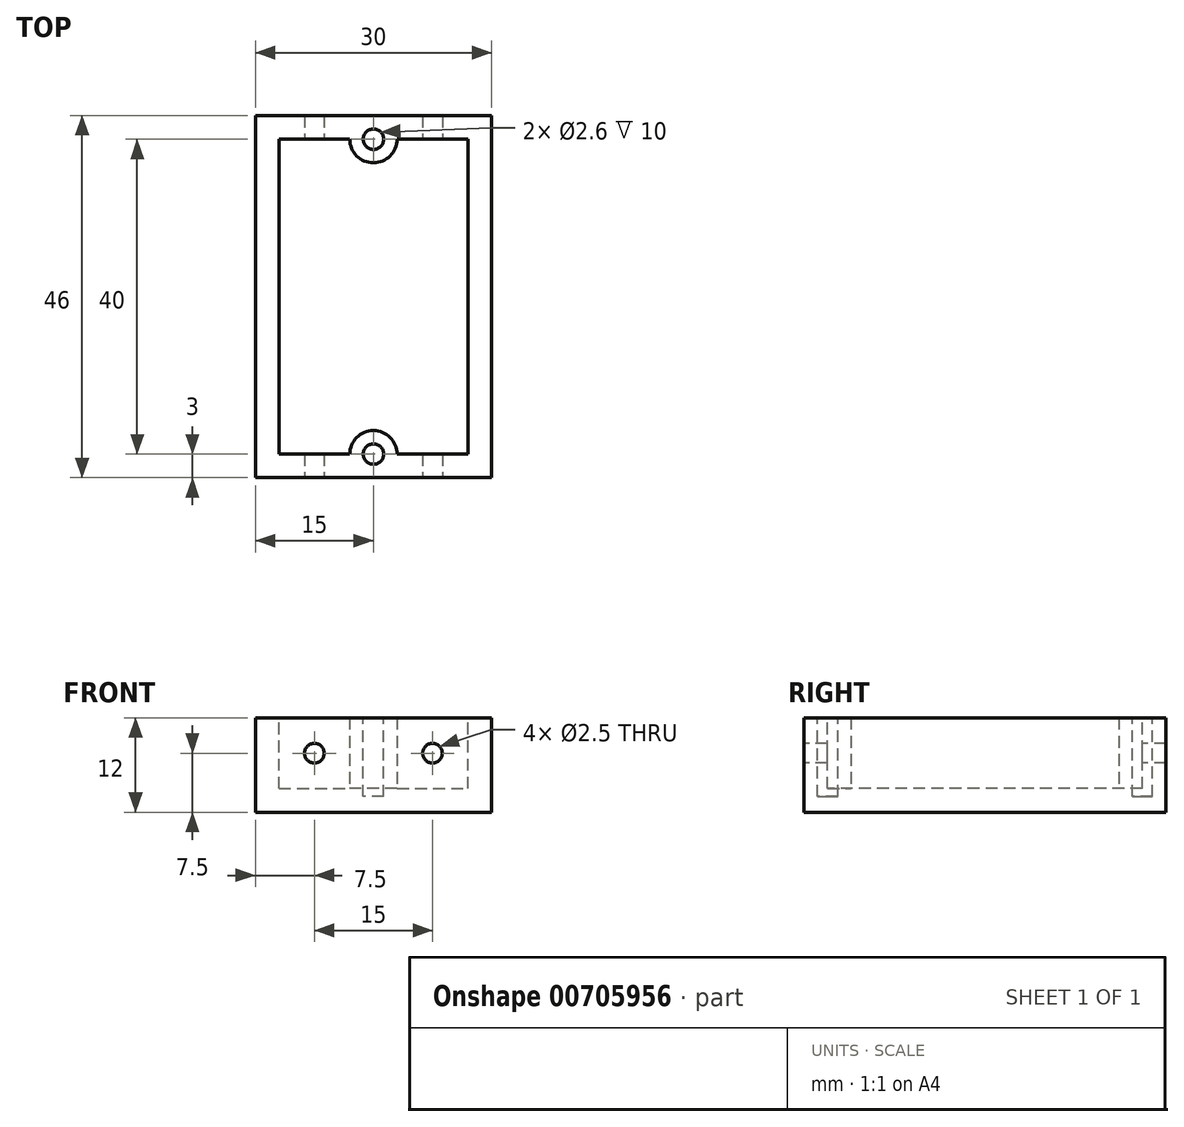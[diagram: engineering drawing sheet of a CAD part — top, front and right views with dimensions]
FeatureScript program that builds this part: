
annotation { "Feature Type Name" : "Feature", "Feature Type Description" : "" }
export const myFeature = defineFeature(function(context is Context, id is Id, definition is map)
    precondition{}
    {
        {
            var Q0;
            Q0=qCreatedBy(makeId("Front.planeOp"),FACE);
            var sketch = newSketch(context, id + "F0", { "sketchPlane" : qUnion([Q0])});
            skLineSegment(sketch, "E0.bottom", {"start": v(15, 7.5) * mm, "end": v(-15, 7.5) * mm});
            skLineSegment(sketch, "E0.top", {"start": v(15, -7.5) * mm, "end": v(-15, -7.5) * mm});
            skLineSegment(sketch, "E0.left", {"start": v(15, 7.5) * mm, "end": v(15, -7.5) * mm});
            skLineSegment(sketch, "E0.right", {"start": v(-15, 7.5) * mm, "end": v(-15, -7.5) * mm});
            skPoint(sketch, "E0.middle", {"position": v(0, 0) * mm});
            skSolve(sketch);
        }
        {
            var Q0;
            Q0=makeQuery(id+"F0.imprint","IMPRINT",FACE,{"disambiguationData":[TD([[makeQuery(id+"F0.imprint","IMPRINT",EDGE,{"derivedFrom":sQuery(id+"F0.wireOp",EDGE,"E0.bottom")}),1.0]])]});
            extrude(context, id + "F1", {"entities" : qUnion([Q0]), "depth" : 46 * mm, "offsetDistance" : 25 * mm});
        }
        {
            var Q0;
            Q0=makeQuery(id+"F1.opExtrude","CAP_FACE",FACE,{"disambiguationData":[OSD([sQuery(id+"F0.wireOp",EDGE,"E0.bottom"),sQuery(id+"F0.wireOp",EDGE,"E0.top"),sQuery(id+"F0.wireOp",EDGE,"E0.left"),sQuery(id+"F0.wireOp",EDGE,"E0.right")])],"isStart":false});
            var sketch = newSketch(context, id + "F2", { "sketchPlane" : qUnion([Q0])});
            skCircle(sketch, "E1", {"center": v(-7.5, 0) * mm, "radius": 1.25 * mm});
            skCircle(sketch, "E2.MirrorC", {"center": v(7.5, 0) * mm, "radius": 1.25 * mm});
            skSolve(sketch);
        }
        {
            var Q0;
            Q0 = qSketchRegion(id + "F2", true);
            extrude(context, id + "F3", {"entities" : qUnion([Q0]), "operationType" : NewBodyOperationType.REMOVE, "endBound" : BoundingType.UP_TO_NEXT, "oppositeDirection" : true, "depth" : 25 * mm, "offsetDistance" : 25 * mm});
        }
        {
            var Q0;
            Q0=makeQuery(id+"F1.opExtrude","SWEPT_FACE",FACE,{"disambiguationData":[OSD([sQuery(id+"F0.wireOp",EDGE,"E0.bottom")])]});
            var sketch = newSketch(context, id + "F4", { "sketchPlane" : qUnion([Q0])});
            skLineSegment(sketch, "E3.bottom", {"start": v(-12, -3) * mm, "end": v(12, -3) * mm});
            skLineSegment(sketch, "E3.top", {"start": v(-12, -43) * mm, "end": v(12, -43) * mm});
            skLineSegment(sketch, "E3.left", {"start": v(-12, -3) * mm, "end": v(-12, -43) * mm});
            skLineSegment(sketch, "E3.right", {"start": v(12, -3) * mm, "end": v(12, -43) * mm});
            skSolve(sketch);
        }
        {
            var Q0;
            Q0 = qSketchRegion(id + "F4", true);
            extrude(context, id + "F5", {"entities" : qUnion([Q0]), "operationType" : NewBodyOperationType.REMOVE, "oppositeDirection" : true, "depth" : 12 * mm, "offsetDistance" : 25 * mm});
        }
        {
            var Q0;
            Q0=makeQuery(id+"F5.boolean.opBoolean","COPY",FACE,{"derivedFrom":makeQuery(id+"F5.opExtrude","CAP_FACE",FACE,{"disambiguationData":[OSD([sQuery(id+"F4.wireOp",EDGE,"E3.bottom"),sQuery(id+"F4.wireOp",EDGE,"E3.top"),sQuery(id+"F4.wireOp",EDGE,"E3.left"),sQuery(id+"F4.wireOp",EDGE,"E3.right")])],"isStart":false})});
            var sketch = newSketch(context, id + "F6", { "sketchPlane" : qUnion([Q0])});
            skCircle(sketch, "E4", {"center": v(0, -3) * mm, "radius": 3 * mm});
            skCircle(sketch, "E5", {"center": v(0, -43) * mm, "radius": 3 * mm});
            skSolve(sketch);
        }
        {
            var Q0;
            Q0 = qSketchRegion(id + "F6", true);
            extrude(context, id + "F7", {"entities" : qUnion([Q0]), "operationType" : NewBodyOperationType.ADD, "depth" : 12 * mm, "offsetDistance" : 25 * mm});
        }
        {
            var Q0;
            Q0=makeQuery(id+"F1.opExtrude","CAP_FACE",FACE,{"disambiguationData":[OSD([sQuery(id+"F0.wireOp",EDGE,"E0.bottom"),sQuery(id+"F0.wireOp",EDGE,"E0.top"),sQuery(id+"F0.wireOp",EDGE,"E0.left"),sQuery(id+"F0.wireOp",EDGE,"E0.right")])],"isStart":true});
            var sketch = newSketch(context, id + "F8", { "sketchPlane" : qUnion([Q0])});
            skLineSegment(sketch, "E6.bottom", {"start": v(-15, 7.5) * mm, "end": v(15, 7.5) * mm});
            skLineSegment(sketch, "E6.top", {"start": v(-15, 4.5) * mm, "end": v(15, 4.5) * mm});
            skLineSegment(sketch, "E6.left", {"start": v(-15, 7.5) * mm, "end": v(-15, 4.5) * mm});
            skLineSegment(sketch, "E6.right", {"start": v(15, 7.5) * mm, "end": v(15, 4.5) * mm});
            skSolve(sketch);
        }
        {
            var Q0;
            Q0 = qSketchRegion(id + "F8", true);
            extrude(context, id + "F9", {"entities" : qUnion([Q0]), "operationType" : NewBodyOperationType.REMOVE, "endBound" : BoundingType.THROUGH_ALL, "oppositeDirection" : true, "depth" : 25 * mm, "offsetDistance" : 25 * mm});
        }
        {
            var Q0;
            Q0=makeQuery(id+"F9.boolean.opBoolean","COPY",FACE,{"derivedFrom":makeQuery(id+"F9.opExtrude","SWEPT_FACE",FACE,{"disambiguationData":[OSD([sQuery(id+"F8.wireOp",EDGE,"E6.top")])]})});
            var sketch = newSketch(context, id + "F10", { "sketchPlane" : qUnion([Q0])});
            skCircle(sketch, "E7", {"center": v(0, -3) * mm, "radius": 1.3 * mm});
            skCircle(sketch, "E8", {"center": v(0, -43) * mm, "radius": 1.3 * mm});
            skSolve(sketch);
        }
        {
            var Q0;
            Q0 = qSketchRegion(id + "F10", true);
            extrude(context, id + "F11", {"entities" : qUnion([Q0]), "operationType" : NewBodyOperationType.REMOVE, "oppositeDirection" : true, "depth" : 10 * mm, "offsetDistance" : 25 * mm});
        }
    });
